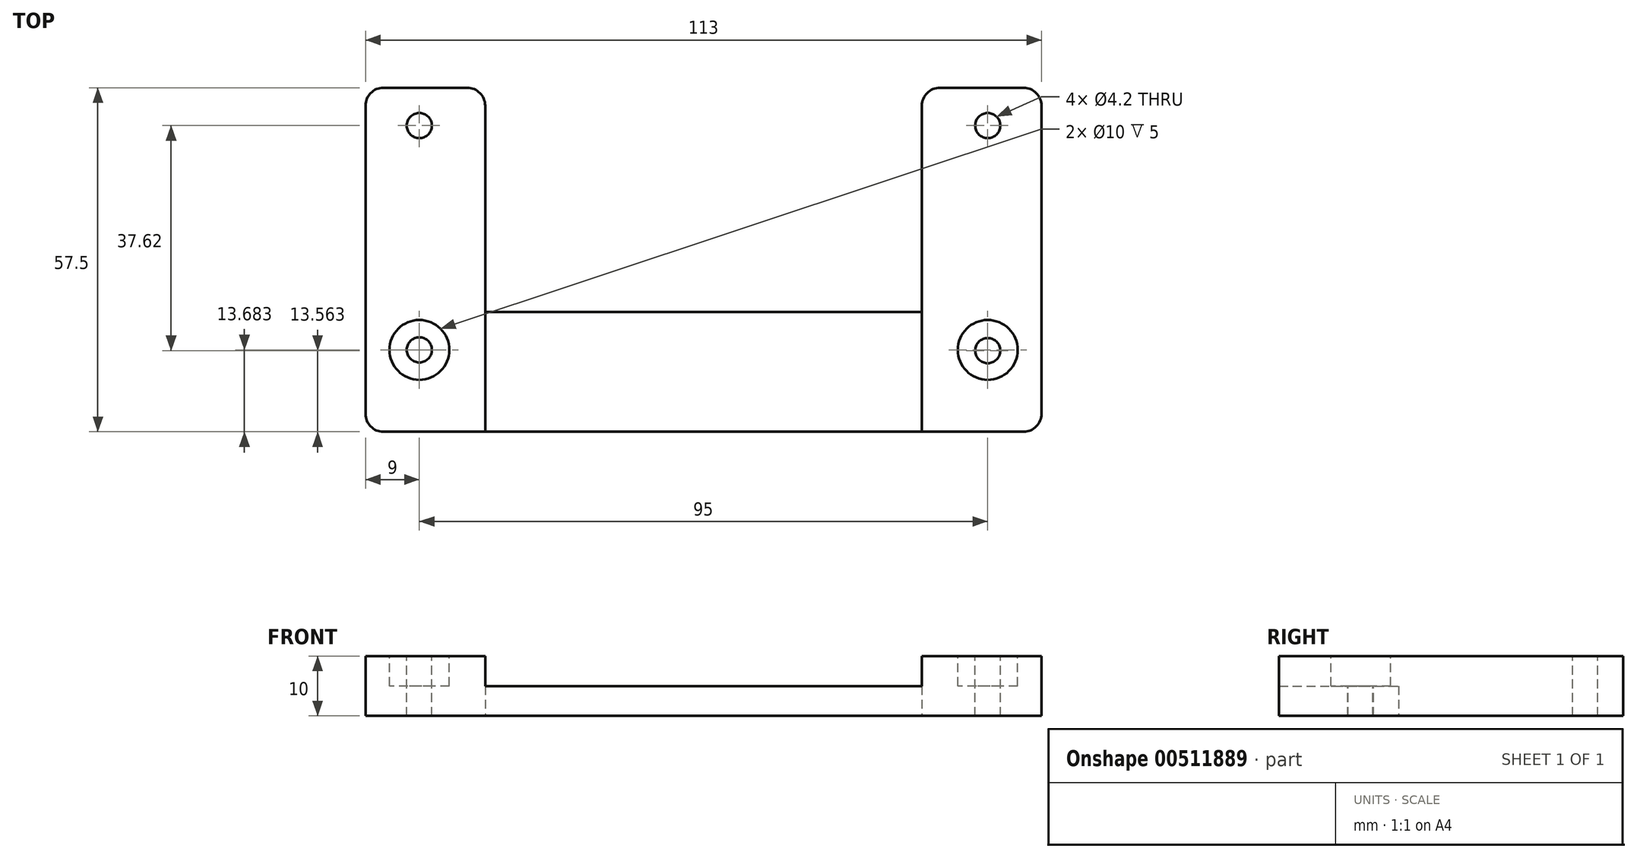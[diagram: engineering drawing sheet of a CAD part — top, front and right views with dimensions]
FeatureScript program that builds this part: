
annotation { "Feature Type Name" : "Feature", "Feature Type Description" : "" }
export const myFeature = defineFeature(function(context is Context, id is Id, definition is map)
    precondition{}
    {
        {
            var Q0;
            Q0=qCreatedBy(makeId("Top.planeOp"),FACE);
            var sketch = newSketch(context, id + "F0", { "sketchPlane" : qUnion([Q0])});
            skLineSegment(sketch, "E0.bottom", {"start": v(0, 0) * mm, "end": v(73, 0) * mm});
            skLineSegment(sketch, "E0.top", {"start": v(0, 20) * mm, "end": v(73, 20) * mm});
            skLineSegment(sketch, "E0.left", {"start": v(0, 0) * mm, "end": v(0, 20) * mm});
            skLineSegment(sketch, "E0.right", {"start": v(73, 0) * mm, "end": v(73, 20) * mm});
            skLineSegment(sketch, "E1.bottom", {"start": v(0, 0) * mm, "end": v(-20, 0) * mm});
            skLineSegment(sketch, "E1.top", {"start": v(0, 57.5) * mm, "end": v(-20, 57.5) * mm});
            skLineSegment(sketch, "E1.left", {"start": v(0, 0) * mm, "end": v(0, 57.5) * mm});
            skLineSegment(sketch, "E1.right", {"start": v(-20, 0) * mm, "end": v(-20, 57.5) * mm});
            skLineSegment(sketch, "E2.bottom", {"start": v(73, 0) * mm, "end": v(93, 0) * mm});
            skLineSegment(sketch, "E2.top", {"start": v(73, 57.5) * mm, "end": v(93, 57.5) * mm});
            skLineSegment(sketch, "E2.left", {"start": v(73, 0) * mm, "end": v(73, 57.5) * mm});
            skLineSegment(sketch, "E2.right", {"start": v(93, 0) * mm, "end": v(93, 57.5) * mm});
            skSolve(sketch);
        }
        {
            var Q0;
            {var subQ3=sQuery(id+"F0.wireOp",EDGE,"E1.bottom");Q0=makeQuery(id+"F0.imprint","IMPRINT",FACE,{"disambiguationData":[TD([[makeQuery(id+"F0.imprint","IMPRINT",EDGE,{"derivedFrom":subQ3}),-1.0]])]});}
            var Q1;
            {var subQ0=sQuery(id+"F0.wireOp",EDGE,"E0.bottom");Q1=makeQuery(id+"F0.imprint","IMPRINT",FACE,{"disambiguationData":[TD([[makeQuery(id+"F0.imprint","IMPRINT",EDGE,{"derivedFrom":subQ0}),1.0]])]});}
            var Q2;
            {var subQ3=sQuery(id+"F0.wireOp",EDGE,"E2.bottom");Q2=makeQuery(id+"F0.imprint","IMPRINT",FACE,{"disambiguationData":[TD([[makeQuery(id+"F0.imprint","IMPRINT",EDGE,{"derivedFrom":subQ3}),1.0]])]});}
            extrude(context, id + "F1", {"entities" : qUnion([Q0, Q1, Q2]), "depth" : 10 * mm});
        }
        {
            var Q0;
            Q0=makeQuery(id+"F1.opExtrude","CAP_FACE",FACE,{"disambiguationData":[OSD([sQuery(id+"F0.wireOp",EDGE,"E0.bottom"),sQuery(id+"F0.wireOp",EDGE,"E0.top"),sQuery(id+"F0.wireOp",EDGE,"E1.bottom"),sQuery(id+"F0.wireOp",EDGE,"E1.top"),sQuery(id+"F0.wireOp",EDGE,"E1.left"),sQuery(id+"F0.wireOp",EDGE,"E1.right"),sQuery(id+"F0.wireOp",EDGE,"E2.bottom"),sQuery(id+"F0.wireOp",EDGE,"E2.top"),sQuery(id+"F0.wireOp",EDGE,"E2.left"),sQuery(id+"F0.wireOp",EDGE,"E2.right")])],"isStart":false});
            var sketch = newSketch(context, id + "F2", { "sketchPlane" : qUnion([Q0])});
            skLineSegment(sketch, "E3.bottom", {"start": v(0, 0) * mm, "end": v(73, 0) * mm});
            skLineSegment(sketch, "E3.top", {"start": v(0, 20) * mm, "end": v(73, 20) * mm});
            skLineSegment(sketch, "E3.left", {"start": v(0, 0) * mm, "end": v(0, 20) * mm});
            skLineSegment(sketch, "E3.right", {"start": v(73, 0) * mm, "end": v(73, 20) * mm});
            skSolve(sketch);
        }
        {
            var Q0;
            Q0=makeQuery(id+"F2.imprint","IMPRINT",FACE,{"disambiguationData":[TD([[makeQuery(id+"F2.imprint","IMPRINT",EDGE,{"derivedFrom":sQuery(id+"F2.wireOp",EDGE,"E3.bottom")}),-1.0]])]});
            extrude(context, id + "F3", {"entities" : qUnion([Q0]), "operationType" : NewBodyOperationType.REMOVE, "oppositeDirection" : true, "depth" : 5 * mm});
        }
        {
            var Q0;
            {var subQ0=sQuery(id+"F0.wireOp",EDGE,"E1.right");var subQ1=sQuery(id+"F0.wireOp",EDGE,"E1.left");var subQ2=sQuery(id+"F0.wireOp",EDGE,"E1.top");var subQ3=sQuery(id+"F0.wireOp",EDGE,"E2.bottom");var subQ4=sQuery(id+"F0.wireOp",EDGE,"E1.bottom");var subQ5=sQuery(id+"F0.wireOp",EDGE,"E0.bottom");Q0=makeQuery(id+"F3.boolean.opBoolean","SPLIT",FACE,{"disambiguationData":[TD([makeQuery(id+"F1.opExtrude","SWEPT_FACE",FACE,{"disambiguationData":[OSD([subQ2])]})])],"derivedFrom":makeQuery(id+"F1.opExtrude","CAP_FACE",FACE,{"disambiguationData":[OSD([subQ5,sQuery(id+"F0.wireOp",EDGE,"E0.top"),subQ4,subQ2,subQ1,subQ0,subQ3,sQuery(id+"F0.wireOp",EDGE,"E2.top"),sQuery(id+"F0.wireOp",EDGE,"E2.left"),sQuery(id+"F0.wireOp",EDGE,"E2.right")])],"isStart":false})});}
            var sketch = newSketch(context, id + "F4", { "sketchPlane" : qUnion([Q0])});
            skCircle(sketch, "E4", {"center": v(-11, 13.68) * mm, "radius": 2.1 * mm});
            skCircle(sketch, "E5", {"center": v(84, 13.56) * mm, "radius": 2.1 * mm});
            skCircle(sketch, "E6", {"center": v(-11, 51.18) * mm, "radius": 2.1 * mm});
            skCircle(sketch, "E7", {"center": v(84, 51.18) * mm, "radius": 2.1 * mm});
            skSolve(sketch);
        }
        {
            var Q0;
            Q0=makeQuery(id+"F4.imprint","IMPRINT",FACE,{"disambiguationData":[TD([[makeQuery(id+"F4.imprint","IMPRINT",EDGE,{"derivedFrom":sQuery(id+"F4.wireOp",EDGE,"E4")}),1.0]])]});
            var Q1;
            Q1=makeQuery(id+"F4.imprint","IMPRINT",FACE,{"disambiguationData":[TD([[makeQuery(id+"F4.imprint","IMPRINT",EDGE,{"derivedFrom":sQuery(id+"F4.wireOp",EDGE,"E5")}),1.0]])]});
            var Q2;
            Q2=makeQuery(id+"F4.imprint","IMPRINT",FACE,{"disambiguationData":[TD([[makeQuery(id+"F4.imprint","IMPRINT",EDGE,{"derivedFrom":sQuery(id+"F4.wireOp",EDGE,"E6")}),1.0]])]});
            var Q3;
            Q3=makeQuery(id+"F4.imprint","IMPRINT",FACE,{"disambiguationData":[TD([[makeQuery(id+"F4.imprint","IMPRINT",EDGE,{"derivedFrom":sQuery(id+"F4.wireOp",EDGE,"E7")}),1.0]])]});
            extrude(context, id + "F5", {"entities" : qUnion([Q0, Q1, Q2, Q3]), "operationType" : NewBodyOperationType.REMOVE, "endBound" : BoundingType.THROUGH_ALL, "oppositeDirection" : true, "depth" : 10 * mm});
        }
        {
            var Q0;
            {var subQ0=sQuery(id+"F0.wireOp",EDGE,"E1.right");var subQ1=sQuery(id+"F0.wireOp",EDGE,"E1.left");var subQ2=sQuery(id+"F0.wireOp",EDGE,"E1.top");var subQ3=sQuery(id+"F0.wireOp",EDGE,"E2.bottom");var subQ4=sQuery(id+"F0.wireOp",EDGE,"E1.bottom");var subQ5=sQuery(id+"F0.wireOp",EDGE,"E0.bottom");Q0=makeQuery(id+"F3.boolean.opBoolean","SPLIT",FACE,{"disambiguationData":[TD([makeQuery(id+"F1.opExtrude","SWEPT_FACE",FACE,{"disambiguationData":[OSD([subQ2])]})])],"derivedFrom":makeQuery(id+"F1.opExtrude","CAP_FACE",FACE,{"disambiguationData":[OSD([subQ5,sQuery(id+"F0.wireOp",EDGE,"E0.top"),subQ4,subQ2,subQ1,subQ0,subQ3,sQuery(id+"F0.wireOp",EDGE,"E2.top"),sQuery(id+"F0.wireOp",EDGE,"E2.left"),sQuery(id+"F0.wireOp",EDGE,"E2.right")])],"isStart":false})});}
            var sketch = newSketch(context, id + "F6", { "sketchPlane" : qUnion([Q0])});
            skCircle(sketch, "E8", {"center": v(-11, 13.68) * mm, "radius": 5 * mm});
            skCircle(sketch, "E9", {"center": v(84, 13.68) * mm, "radius": 5 * mm});
            skSolve(sketch);
        }
        {
            var Q0;
            Q0=makeQuery(id+"F6.imprint","IMPRINT",FACE,{"disambiguationData":[TD([[makeQuery(id+"F6.imprint","IMPRINT",EDGE,{"derivedFrom":sQuery(id+"F6.wireOp",EDGE,"E8")}),1.0]])]});
            var Q1;
            Q1=makeQuery(id+"F6.imprint","IMPRINT",FACE,{"disambiguationData":[TD([[makeQuery(id+"F6.imprint","IMPRINT",EDGE,{"derivedFrom":sQuery(id+"F6.wireOp",EDGE,"E9")}),1.0]])]});
            extrude(context, id + "F7", {"entities" : qUnion([Q0, Q1]), "operationType" : NewBodyOperationType.REMOVE, "oppositeDirection" : true, "depth" : 5 * mm});
        }
        {
            var Q0;
            Q0=makeQuery(id+"F1.opExtrude","SWEPT_EDGE",EDGE,{"disambiguationData":[OSD([sQuery(id+"F0.wireOp",EDGE,"E1.top"),sQuery(id+"F0.wireOp",EDGE,"E1.right")])]});
            var Q1;
            Q1=makeQuery(id+"F1.opExtrude","SWEPT_EDGE",EDGE,{"disambiguationData":[OSD([sQuery(id+"F0.wireOp",EDGE,"E1.top"),sQuery(id+"F0.wireOp",EDGE,"E1.left")])]});
            var Q2;
            Q2=makeQuery(id+"F1.opExtrude","SWEPT_EDGE",EDGE,{"disambiguationData":[OSD([sQuery(id+"F0.wireOp",EDGE,"E2.top"),sQuery(id+"F0.wireOp",EDGE,"E2.left")])]});
            var Q3;
            Q3=makeQuery(id+"F1.opExtrude","SWEPT_EDGE",EDGE,{"disambiguationData":[OSD([sQuery(id+"F0.wireOp",EDGE,"E2.top"),sQuery(id+"F0.wireOp",EDGE,"E2.right")])]});
            var Q4;
            Q4=makeQuery(id+"F1.opExtrude","SWEPT_EDGE",EDGE,{"disambiguationData":[OSD([sQuery(id+"F0.wireOp",EDGE,"E1.bottom"),sQuery(id+"F0.wireOp",EDGE,"E1.right")])]});
            var Q5;
            Q5=makeQuery(id+"F1.opExtrude","SWEPT_EDGE",EDGE,{"disambiguationData":[OSD([sQuery(id+"F0.wireOp",EDGE,"E2.bottom"),sQuery(id+"F0.wireOp",EDGE,"E2.right")])]});
            var Q6;
            Q6=makeQuery(id+"F3.boolean.opBoolean","COPY",EDGE,{"derivedFrom":makeQuery(id+"F3.opExtrude","SWEPT_EDGE",EDGE,{"disambiguationData":[OSD([sQuery(id+"F0.wireOp",EDGE,"E0.bottom"),sQuery(id+"F0.wireOp",EDGE,"E1.bottom"),sQuery(id+"F0.wireOp",EDGE,"E2.bottom"),sQuery(id+"F2.wireOp",EDGE,"E3.bottom"),sQuery(id+"F2.wireOp",EDGE,"E3.left")])]})});
            var Q7;
            Q7=makeQuery(id+"F3.boolean.opBoolean","COPY",EDGE,{"derivedFrom":makeQuery(id+"F3.opExtrude","SWEPT_EDGE",EDGE,{"disambiguationData":[OSD([sQuery(id+"F0.wireOp",EDGE,"E0.bottom"),sQuery(id+"F0.wireOp",EDGE,"E1.bottom"),sQuery(id+"F0.wireOp",EDGE,"E2.bottom"),sQuery(id+"F2.wireOp",EDGE,"E3.bottom"),sQuery(id+"F2.wireOp",EDGE,"E3.right")])]})});
            fillet(context, id + "F8", {"entities" : qUnion([Q0, Q1, Q2, Q3, Q4, Q5, Q6, Q7]), "radius" : 3 * mm, "tangentPropagation" : true, "allowEdgeOverflow" : false});
        }
    });
